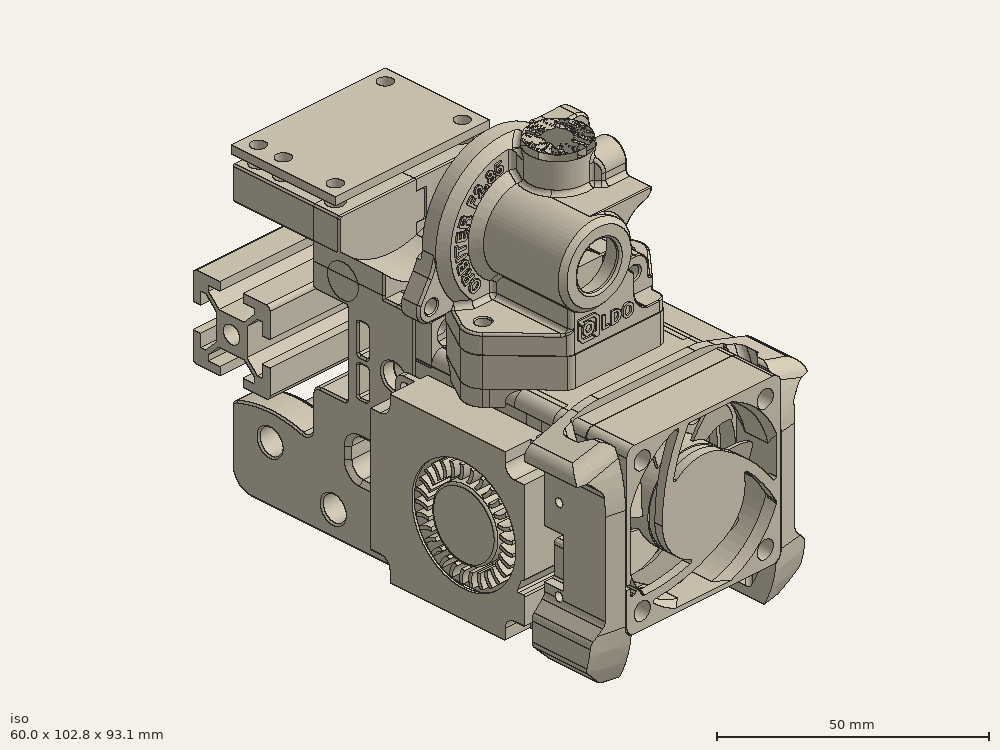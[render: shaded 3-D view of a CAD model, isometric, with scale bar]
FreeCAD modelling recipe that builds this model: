
FCSTD DOCUMENT  (FreeCAD 0.19R24291 (Git))
Label: dual4010-orbitor
License: Other
LicenseURL: GPL3
objects: Part::Cylinder×59, Part::MultiFuse×51, Part::Cut×51, Part::Box×46, Part::Feature×33, Part::Fillet×9, Part::Chamfer×9, Mesh::Feature×1, Part::Extrusion×1, Part::MultiCommon×1
note: 260 computed .brp shape members not serialized (recipe doc carries the construction recipe); baked Part::Feature solids carry a one-line shape summary decoded from their .brp

FEATURE [Part::Feature] Part__Feature376001  label="Left"
  shape: bbox 22.08 x 49.92 x 69.17 mm, 332 faces (baked)
FEATURE [Part::Feature] Part__Feature377001  label="Right"
  shape: bbox 22.32 x 49.92 x 69.17 mm, 357 faces (baked)
FEATURE [Part::Feature] Fusion003  label="mosquito"
  Placement = pos=(9e-15,-17.6,10) rot=(0.57735,0.57735,0.57735;2.0944rad)
  shape: bbox 27 x 18.85 x 47 mm, 463 faces, 0 solids (baked)
FEATURE [Part::Feature] Fusion036012039008  label="_2510-fan-pref"
  Placement = pos=(0.02,-24.2,26) rot=(1,0,0;1.5708rad)
  shape: bbox 25.76 x 10.5 x 25.8 mm, 132 faces, 2 solids (baked)
FEATURE [Part::Feature] Fusion001001  label="4010-fan"
  Placement = pos=(-19.9,-18.6,4.7) rot=(0,0,-1;1.5708rad)
  shape: bbox 10 x 40 x 40 mm, 256 faces, 2 solids (baked)
FEATURE [Part::Feature] Fusion036012039009  label="4010-fan001"
  Placement = pos=(19.9,-18.5,4.6) rot=(0,0,1;1.5708rad)
  shape: bbox 10 x 40 x 40 mm, 256 faces, 2 solids (baked)
FEATURE [Mesh::Feature] orbitor2
  Placement = pos=(-6.35,-7.9,74.9) rot=(0,0,1;0rad)
FEATURE [Part::Feature] Part__Feature013001  label="Cooling Fan Duct Focussed Edition_003"
  shape: bbox 15.53 x 56.74 x 51.73 mm, 120 faces (baked)
FEATURE [Part::Feature] Part__Feature012001  label="Cooling Fan Duct Focussed Edition001"
  shape: bbox 15.53 x 56.74 x 51.73 mm, 120 faces (baked)
FEATURE [Part::Feature] Part__Feature014001001  label="V6 Toolhead Mount 005"
  Placement = pos=(-0.05,0,0) rot=(0,0,1;0rad)
  shape: bbox 51.21 x 26.02 x 49.91 mm, 255 faces (baked)
FEATURE [Part::Box] Box  label="Cube"
  AttacherType = Attacher::AttachEngine3D
  Height = 10
  Length = 66
  Placement = pos=(-34,-27,49.86) rot=(0,0,1;0rad)
  Width = 34
FEATURE [Part::Box] Box002  label="Cube001"
  AttacherType = Attacher::AttachEngine3D
  Height = 10
  Length = 10
  Placement = pos=(-30,-23,41) rot=(0,0,1;0rad)
  Width = 26
FEATURE [Part::Box] Box004  label="Cube003"
  AttacherType = Attacher::AttachEngine3D
  Height = 10
  Length = 10
  Placement = pos=(20,-23,41) rot=(0,0,1;0rad)
  Width = 26
FEATURE [Part::Box] Box005  label="Cube004"
  AttacherType = Attacher::AttachEngine3D
  Height = 5.59
  Length = 24
  Placement = pos=(-12,-21.61,44.26) rot=(0,0,1;0rad)
  Width = 21.6
FEATURE [Part::Box] Box009  label="Cube008"
  AttacherType = Attacher::AttachEngine3D
  Height = 1.5
  Length = 24
  Placement = pos=(-12,-21.61,10.56) rot=(0,0,1;0rad)
  Width = 16
FEATURE [Part::Box] Box010  label="Cube009"
  AttacherType = Attacher::AttachEngine3D
  Height = 10
  Length = 25.3
  Placement = pos=(-12.65,-26.15,9.85) rot=(0,0,1;0rad)
  Width = 15
FEATURE [Part::Box] Box007  label="Cube006"
  AttacherType = Attacher::AttachEngine3D
  Height = 6
  Length = 30.3
  Placement = pos=(-15.15,-21.61,38.5) rot=(0,0,1;0rad)
  Width = 21.6
FEATURE [Part::Cylinder] Cylinder
  Angle = 360
  AttacherType = Attacher::AttachEngine3D
  Height = 22
  Placement = pos=(0,-17.6,33) rot=(0,0,1;0rad)
  Radius = 2.15
FEATURE [Part::Cylinder] Cylinder001
  Angle = 360
  AttacherType = Attacher::AttachEngine3D
  Height = 5
  Placement = pos=(-6,-17.6,33) rot=(0,0,1;0rad)
  Radius = 2.7
FEATURE [Part::Cylinder] Cylinder002
  Angle = 360
  AttacherType = Attacher::AttachEngine3D
  Height = 5
  Placement = pos=(6,-17.6,33) rot=(0,0,1;0rad)
  Radius = 2.7
FEATURE [Part::Cylinder] Cylinder003
  Angle = 360
  AttacherType = Attacher::AttachEngine3D
  Height = 22
  Placement = pos=(6,-17.6,33) rot=(0,0,1;0rad)
  Radius = 1.3
FEATURE [Part::Cylinder] Cylinder004
  Angle = 360
  AttacherType = Attacher::AttachEngine3D
  Height = 22
  Placement = pos=(-6,-17.6,33) rot=(0,0,1;0rad)
  Radius = 1.3
FEATURE [Part::MultiFuse] Fusion036012039011
  Shapes = -> [Cylinder,Cylinder003,Cylinder004]
FEATURE [Part::MultiFuse] Fusion036012039012
  Placement = pos=(0,0,11.9) rot=(0,0,1;0rad)
  Shapes = -> [Cylinder001,Cylinder002]
FEATURE [Part::Box] Box011  label="Cube010"
  AttacherType = Attacher::AttachEngine3D
  Height = 4.5
  Length = 12.15
  Placement = pos=(-18.65,-11.15,14) rot=(0,0,1;0rad)
  Width = 11.14
FEATURE [Part::Box] Box012  label="Cube011"
  AttacherType = Attacher::AttachEngine3D
  Height = 4.5
  Length = 12.15
  Placement = pos=(6.5,-11.15,14) rot=(0,0,1;0rad)
  Width = 11.14
FEATURE [Part::Box] Box013  label="Cube012"
  AttacherType = Attacher::AttachEngine3D
  Height = 10
  Length = 23.6
  Placement = pos=(-11.8,-22,4) rot=(0,0,1;0rad)
  Width = 11
FEATURE [Part::Fillet] Fillet
  Base = -> Box013
  Edges = 2 edges r=3: [Edge3,Edge7]
  Placement = pos=(0,2,0) rot=(0,0,1;0rad)
FEATURE [Part::Cylinder] Cylinder005
  Angle = 360
  AttacherType = Attacher::AttachEngine3D
  Height = 7
  Placement = pos=(16.1,-35.5,14.36) rot=(1,0,0;1.5708rad)
  Radius = 2.05
FEATURE [Part::Cylinder] Cylinder008
  Angle = 360
  AttacherType = Attacher::AttachEngine3D
  Height = 7
  Placement = pos=(-16.1,-35.5,14.36) rot=(1,0,0;1.5708rad)
  Radius = 2.05
FEATURE [Part::Cylinder] Cylinder009
  Angle = 360
  AttacherType = Attacher::AttachEngine3D
  Height = 8
  Placement = pos=(-16.1,-35.5,14.36) rot=(1,0,0;1.5708rad)
  Radius = 3.4
FEATURE [Part::Cylinder] Cylinder010
  Angle = 360
  AttacherType = Attacher::AttachEngine3D
  Height = 8
  Placement = pos=(-16.1,-35.5,46.21) rot=(1,0,0;1.5708rad)
  Radius = 3.4
FEATURE [Part::Cylinder] Cylinder011
  Angle = 360
  AttacherType = Attacher::AttachEngine3D
  Height = 8
  Placement = pos=(16.1,-35.5,46.21) rot=(1,0,0;1.5708rad)
  Radius = 3.4
FEATURE [Part::Cylinder] Cylinder012
  Angle = 360
  AttacherType = Attacher::AttachEngine3D
  Height = 8
  Placement = pos=(16.1,-35.5,14.36) rot=(1,0,0;1.5708rad)
  Radius = 3.4
FEATURE [Part::Cylinder] Cylinder013
  Angle = 360
  AttacherType = Attacher::AttachEngine3D
  Height = 21.6
  Placement = pos=(-16.1,-35.5,14.36) rot=(1,0,0;1.5708rad)
  Radius = 2
FEATURE [Part::Cylinder] Cylinder014
  Angle = 360
  AttacherType = Attacher::AttachEngine3D
  Height = 21.6
  Placement = pos=(-16.1,-35.5,46.21) rot=(1,0,0;1.5708rad)
  Radius = 2
FEATURE [Part::Cylinder] Cylinder015
  Angle = 360
  AttacherType = Attacher::AttachEngine3D
  Height = 21.6
  Placement = pos=(16.1,-35.5,46.21) rot=(1,0,0;1.5708rad)
  Radius = 2
FEATURE [Part::Cylinder] Cylinder016
  Angle = 360
  AttacherType = Attacher::AttachEngine3D
  Height = 21.6
  Placement = pos=(16.1,-35.5,14.36) rot=(1,0,0;1.5708rad)
  Radius = 2
FEATURE [Part::MultiFuse] Fusion036012039014
  Placement = pos=(0,35.49,0) rot=(0,0,1;0rad)
  Shapes = -> [Cylinder016,Cylinder015,Cylinder014,Cylinder013]
FEATURE [Part::MultiFuse] Fusion036012039016
  Placement = pos=(0,35.49,0) rot=(0,0,1;0rad)
  Shapes = -> [Cylinder012,Cylinder011,Cylinder010,Cylinder009]
FEATURE [Part::Cylinder] Cylinder017
  Angle = 360
  AttacherType = Attacher::AttachEngine3D
  Height = 10
  Placement = pos=(16.1,-35.5,14.36) rot=(1,0,0;1.5708rad)
  Radius = 1.7
FEATURE [Part::Cylinder] Cylinder019
  Angle = 360
  AttacherType = Attacher::AttachEngine3D
  Height = 10
  Placement = pos=(-16.1,-35.5,14.36) rot=(1,0,0;1.5708rad)
  Radius = 1.7
FEATURE [Part::Box] Box016  label="Cube015"
  AttacherType = Attacher::AttachEngine3D
  Height = 7
  Length = 1.2
  Placement = pos=(18.8,-21.61,42.8) rot=(0,0,1;0rad)
  Width = 14
FEATURE [Part::MultiFuse] Fusion036012039022
  Placement = pos=(0,23.89,0) rot=(0,0,1;0rad)
  Shapes = -> [Cylinder019,Cylinder017]
FEATURE [Part::MultiFuse] Fusion036012039023
  Placement = pos=(0,20.89,0) rot=(0,0,1;0rad)
  Shapes = -> [Cylinder005,Cylinder008]
FEATURE [Part::Cylinder] Cylinder020
  Angle = 360
  AttacherType = Attacher::AttachEngine3D
  Height = 10
  Placement = pos=(17.05,7,34) rot=(0.57735,-0.57735,0.57735;2.0944rad)
  Radius = 2.05
FEATURE [Part::Cylinder] Cylinder021
  Angle = 360
  AttacherType = Attacher::AttachEngine3D
  Height = 10
  Placement = pos=(-17.05,7,34) rot=(0.57735,-0.57735,0.57735;2.0944rad)
  Radius = 2.05
FEATURE [Part::Cylinder] Cylinder022
  Angle = 360
  AttacherType = Attacher::AttachEngine3D
  Height = 22.2
  Placement = pos=(-17.05,0,34) rot=(0.57735,-0.57735,0.57735;2.0944rad)
  Radius = 1.65
FEATURE [Part::Cylinder] Cylinder023
  Angle = 360
  AttacherType = Attacher::AttachEngine3D
  Height = 22.2
  Placement = pos=(17.05,8e-15,34) rot=(0.57735,-0.57735,0.57735;2.0944rad)
  Radius = 1.65
FEATURE [Part::Cylinder] Cylinder024
  Angle = 360
  AttacherType = Attacher::AttachEngine3D
  Height = 16
  Placement = pos=(-17.05,0,34) rot=(0.57735,-0.57735,0.57735;2.0944rad)
  Radius = 4
FEATURE [Part::Cylinder] Cylinder025
  Angle = 360
  AttacherType = Attacher::AttachEngine3D
  Height = 16
  Placement = pos=(17.05,8e-15,34) rot=(0.57735,-0.57735,0.57735;2.0944rad)
  Radius = 4
FEATURE [Part::Cut] Cut009
  Base = -> Part__Feature376001
  Tool = -> Cylinder021
FEATURE [Part::Box] Box017  label="Cube016"
  AttacherType = Attacher::AttachEngine3D
  Height = 10
  Length = 10
  Placement = pos=(17.9,-16,29) rot=(0,0,1;0rad)
  Width = 26
FEATURE [Part::Box] Box018  label="Cube017"
  AttacherType = Attacher::AttachEngine3D
  Height = 10
  Length = 10
  Placement = pos=(-27.9,-16,29) rot=(0,0,1;0rad)
  Width = 26
FEATURE [Part::MultiFuse] Fusion036012039026
  Shapes = -> [Box017,Box018]
FEATURE [Part::Cut] Cut
  Base = -> Part__Feature014001001
  Tool = -> Box
FEATURE [Part::MultiFuse] Fusion036012039033
  Shapes = -> [Box011,Box012]
FEATURE [Part::Cylinder] Cylinder030
  Angle = 360
  AttacherType = Attacher::AttachEngine3D
  Height = 11
  Placement = pos=(16.25,11,9.41) rot=(1,0,0;1.5708rad)
  Radius = 2.5
FEATURE [Part::Cylinder] Cylinder031
  Angle = 360
  AttacherType = Attacher::AttachEngine3D
  Height = 11
  Placement = pos=(-16.25,11,9.41) rot=(1,0,0;1.5708rad)
  Radius = 2.5
FEATURE [Part::MultiFuse] Fusion036012039039
  Shapes = -> [Cut009,Cylinder031]
FEATURE [Part::Box] Box019  label="Cube018"
  AttacherType = Attacher::AttachEngine3D
  Height = 10
  Length = 8.8
  Placement = pos=(11.2,-5,5) rot=(0,0,1;0rad)
  Width = 5
FEATURE [Part::Box] Box020  label="Cube019"
  AttacherType = Attacher::AttachEngine3D
  Height = 10
  Length = 8.8
  Placement = pos=(-20,-5,5) rot=(0,0,1;0rad)
  Width = 5
FEATURE [Part::Chamfer] Chamfer002
  Base = -> Box019
  Edges = 5 edges r=0.4: [Edge3,Edge4,Edge7,Edge8,Edge11]
FEATURE [Part::Chamfer] Chamfer003
  Base = -> Box020
  Edges = 5 edges r=0.4: [Edge3,Edge4,Edge7,Edge8,Edge11]
FEATURE [Part::Box] Box021  label="Cube020"
  AttacherType = Attacher::AttachEngine3D
  Height = 10
  Length = 26
  Placement = pos=(-13,-10,10.6) rot=(0,0,1;0rad)
  Width = 10
FEATURE [Part::Cylinder] Cylinder032
  Angle = 360
  AttacherType = Attacher::AttachEngine3D
  Height = 10
  Placement = pos=(-15.6,7,7.5) rot=(0.57735,-0.57735,0.57735;2.0944rad)
  Radius = 2.05
FEATURE [Part::Cylinder] Cylinder033
  Angle = 360
  AttacherType = Attacher::AttachEngine3D
  Height = 10
  Placement = pos=(15.6,7,7.5) rot=(0.57735,-0.57735,0.57735;2.0944rad)
  Radius = 2.05
FEATURE [Part::Cylinder] Cylinder034
  Angle = 360
  AttacherType = Attacher::AttachEngine3D
  Height = 10
  Placement = pos=(-15.6,2e-15,7.5) rot=(0.57735,-0.57735,0.57735;2.0944rad)
  Radius = 1.65
FEATURE [Part::Cylinder] Cylinder035
  Angle = 360
  AttacherType = Attacher::AttachEngine3D
  Height = 10
  Placement = pos=(15.6,0,7.5) rot=(0.57735,-0.57735,0.57735;2.0944rad)
  Radius = 1.65
FEATURE [Part::MultiFuse] Fusion036012039042
  Placement = pos=(0,3,0) rot=(0,0,1;0rad)
  Shapes = -> [Cylinder035,Cylinder034]
FEATURE [Part::MultiFuse] Fusion036012039043
  Shapes = -> [Chamfer003,Chamfer002]
FEATURE [Part::Cut] Cut021
  Base = -> Fusion036012039043
  Tool = -> Box021
FEATURE [Part::Cut] Cut023
  Base = -> Fusion036012039039
  Tool = -> Cylinder032
FEATURE [Part::Box] Box023  label="Cube022"
  AttacherType = Attacher::AttachEngine3D
  Height = 10
  Length = 3.3
  Placement = pos=(-17.25,-6,-2.5) rot=(0,0,1;0rad)
  Width = 10
FEATURE [Part::Box] Box024  label="Cube023"
  AttacherType = Attacher::AttachEngine3D
  Height = 10
  Length = 3.3
  Placement = pos=(13.95,-8,-2.5) rot=(0,0,1;0rad)
  Width = 10
FEATURE [Part::MultiFuse] Fusion036012039045
  Shapes = -> [Box023,Box024]
FEATURE [Part::MultiFuse] Fusion036012039029004
  Shapes = -> [Fusion036012039045,Fusion036012039042]
FEATURE [Part::Box] Box028  label="Cube027"
  AttacherType = Attacher::AttachEngine3D
  Height = 4
  Length = 2
  Placement = pos=(18,-25,16) rot=(0,0,1;0rad)
  Width = 22
FEATURE [Part::Fillet] Fillet001
  Base = -> Box028
  Edges = 2 edges r=1: [Edge11,Edge12]
  Placement = pos=(0.8,-0.6,0) rot=(0,0,1;0rad)
FEATURE [Part::Box] Box030  label="Cube029"
  AttacherType = Attacher::AttachEngine3D
  Height = 28
  Length = 1.2
  Placement = pos=(18.8,-21.61,15.8) rot=(0,0,1;0rad)
  Width = 18
FEATURE [Part::Box] Box031  label="Cube030"
  AttacherType = Attacher::AttachEngine3D
  Height = 8
  Length = 2
  Placement = pos=(18.8,-7.61,17.9) rot=(0,0,1;0rad)
  Width = 4
FEATURE [Part::Feature] Part__Feature034  label="4010-fan002"
  Placement = pos=(-19.975,-55.3,50.05) rot=(0.57735,0.57735,-0.57735;2.0944rad)
  shape: bbox 40.01 x 10.74 x 40.01 mm, 116 faces (baked)
FEATURE [Part::Cylinder] Cylinder037
  Angle = 360
  AttacherType = Attacher::AttachEngine3D
  Height = 20
  Placement = pos=(-9e-15,18.55,55.65) rot=(0.707107,0,0.707107;3.14159rad)
  Radius = 4
FEATURE [Part::Cylinder] Cylinder038
  Angle = 360
  AttacherType = Attacher::AttachEngine3D
  Height = 20
  Placement = pos=(-20,18.55,55.65) rot=(0.707107,0,0.707107;3.14159rad)
  Radius = 4
FEATURE [Part::MultiFuse] Fusion036012039029011  label="Fusion036012039029012"
  Shapes = -> [Cut023,Cylinder038]
FEATURE [Part::Box] Box036  label="Cube035"
  AttacherType = Attacher::AttachEngine3D
  Height = 14
  Length = 60
  Placement = pos=(-30,19.3,56.3) rot=(0,0,1;0rad)
  Width = 36
FEATURE [Part::Feature] Chamfer008016001  label="m8-probe-mount001"
  Placement = pos=(0,10,3) rot=(0,0,1;0rad)
  shape: bbox 15 x 15.5 x 10 mm, 61 faces (baked)
FEATURE [Part::Box] Box040  label="Cube039"
  AttacherType = Attacher::AttachEngine3D
  Height = 9.8
  Length = 9.2
  Placement = pos=(-20,-4.51,46.5) rot=(0,0,1;0rad)
  Width = 4.5
FEATURE [Part::Box] Box041  label="Cube040"
  AttacherType = Attacher::AttachEngine3D
  Height = 9.8
  Length = 9.2
  Placement = pos=(10.8,-4.51,46.5) rot=(0,0,1;0rad)
  Width = 4.5
FEATURE [Part::Box] Box042  label="Cube041"
  AttacherType = Attacher::AttachEngine3D
  Height = 14
  Length = 21.6
  Placement = pos=(-10.8,-10.95,38) rot=(0,0,1;0rad)
  Width = 15
FEATURE [Part::Box] Box043  label="Cube042"
  AttacherType = Attacher::AttachEngine3D
  Height = 10
  Length = 10
  Placement = pos=(-27,-23,46.86) rot=(0,0,1;0rad)
  Width = 24
FEATURE [Part::Box] Box044  label="Cube043"
  AttacherType = Attacher::AttachEngine3D
  Height = 10
  Length = 10
  Placement = pos=(17,-23,46.86) rot=(0,0,1;0rad)
  Width = 24
FEATURE [Part::Box] Box045  label="Cube044"
  AttacherType = Attacher::AttachEngine3D
  Height = 10
  Length = 10
  Placement = pos=(-20,-23,39.86) rot=(0,0,1;0rad)
  Width = 24
FEATURE [Part::Box] Box046  label="Cube045"
  AttacherType = Attacher::AttachEngine3D
  Height = 10
  Length = 10
  Placement = pos=(10,-23,39.86) rot=(0,0,1;0rad)
  Width = 24
FEATURE [Part::Fillet] Fillet001005
  Base = -> Box045
  Edges = 1 edges r=2.8: [Edge2]
FEATURE [Part::Fillet] Fillet001006
  Base = -> Box046
  Edges = 1 edges r=2.8: [Edge6]
FEATURE [Part::Cut] Cut011025
  Base = -> Box043
  Tool = -> Fillet001005
FEATURE [Part::Cut] Cut011026
  Base = -> Box044
  Tool = -> Fillet001006
FEATURE [Part::MultiFuse] Fusion036012039029016  label="Fusion036012039029017"
  Shapes = -> [Cut011026,Cut011025]
FEATURE [Part::Chamfer] Chamfer008016002
  Base = -> Box041
  Edges = 5 edges r=0.4: [Edge2,Edge3,Edge6,Edge7,Edge12]
FEATURE [Part::Chamfer] Chamfer008016003
  Base = -> Box040
  Edges = 5 edges r=0.4: [Edge2,Edge3,Edge6,Edge7,Edge12]
FEATURE [Part::MultiFuse] Fusion036012039029017  label="Fusion036012039029018"
  Shapes = -> [Chamfer008016002,Chamfer008016003]
FEATURE [Part::Cylinder] Cylinder041
  Angle = 360
  AttacherType = Attacher::AttachEngine3D
  Height = 10
  Placement = pos=(15.5,-2.5,52.71) rot=(1,0,0;1.5708rad)
  Radius = 3
FEATURE [Part::Cylinder] Cylinder042
  Angle = 360
  AttacherType = Attacher::AttachEngine3D
  Height = 10
  Placement = pos=(-15.5,-2.5,52.71) rot=(1,0,0;1.5708rad)
  Radius = 3
FEATURE [Part::Cylinder] Cylinder043
  Angle = 360
  AttacherType = Attacher::AttachEngine3D
  Height = 10
  Placement = pos=(-15.5,7,52.71) rot=(1,0,0;1.5708rad)
  Radius = 2.05
FEATURE [Part::Cylinder] Cylinder044
  Angle = 360
  AttacherType = Attacher::AttachEngine3D
  Height = 10
  Placement = pos=(15.5,7,52.71) rot=(1,0,0;1.5708rad)
  Radius = 2.05
FEATURE [Part::Cylinder] Cylinder045
  Angle = 360
  AttacherType = Attacher::AttachEngine3D
  Height = 10
  Placement = pos=(-15.5,1.2e-14,52.71) rot=(1,0,0;1.5708rad)
  Radius = 1.65
FEATURE [Part::Cylinder] Cylinder046
  Angle = 360
  AttacherType = Attacher::AttachEngine3D
  Height = 10
  Placement = pos=(15.5,1.2e-14,52.71) rot=(1,0,0;1.5708rad)
  Radius = 1.65
FEATURE [Part::Feature] Fillet001016001  label="front-body-r1"
  shape: bbox 104.4 x 16.9 x 53 mm, 125 faces (baked)
FEATURE [Part::Feature] Fillet001013001  label="fan-spacer-r1"
  shape: bbox 40 x 4 x 40 mm, 20 faces (baked)
FEATURE [Part::MultiFuse] Fusion
  Shapes = -> [Box002,Box004]
FEATURE [Part::Cut] Cut011033
  Base = -> Cut
  Tool = -> Fusion
FEATURE [Part::MultiFuse] Fusion036012039029018  label="Fusion036012039029019"
  Shapes = -> [Cut011033,Box005]
FEATURE [Part::MultiFuse] Fusion036012039029019  label="Fusion036012039029020"
  Shapes = -> [Box009,Fusion036012039029018]
FEATURE [Part::Cut] Cut011034
  Base = -> Fusion036012039029019
  Tool = -> Box010
FEATURE [Part::Chamfer] Chamfer
  Base = -> Fusion036012039033
  Edges = 2 edges r=5: [Edge7,Edge15]
FEATURE [Part::Chamfer] Chamfer008016004
  Base = -> Chamfer
  Edges = 2 edges r=0.4: [Edge3,Edge18]
FEATURE [Part::Box] Box047  label="Cube046"
  AttacherType = Attacher::AttachEngine3D
  Height = 8
  Length = 2
  Placement = pos=(18.8,-25.61,17.9) rot=(0,0,1;0rad)
  Width = 4
FEATURE [Part::Fillet] Fillet001016002
  Base = -> Box031
  Edges = 2 edges r=1: [Edge10,Edge12]
FEATURE [Part::MultiFuse] Fusion036012039029029  label="Fusion036012039029030"
  Shapes = -> [Fillet001,Box047,Fillet001016002]
FEATURE [Part::Fillet] Fillet001016003
  Base = -> Fusion036012039029029
  Edges = 2 edges r=1: [Edge11,Edge21]
FEATURE [Part::MultiFuse] Fusion036012039029031  label="Fusion036012039029032"
  Shapes = -> [Cylinder042,Cylinder041,Cylinder045,Cylinder046]
FEATURE [Part::Feature] Part__Feature082001  label="orbitor-front-body"
  Placement = pos=(-6.58,-4.85,74.86) rot=(0,0,1;3.14159rad)
  shape: bbox 135.7 x 30.33 x 139 mm, 688 faces (baked)
FEATURE [Part::Cylinder] Cylinder047
  Angle = 360
  AttacherType = Attacher::AttachEngine3D
  Height = 10
  Placement = pos=(-19.5,-17.6,46) rot=(0,0,1;0rad)
  Radius = 2
FEATURE [Part::Cylinder] Cylinder048
  Angle = 360
  AttacherType = Attacher::AttachEngine3D
  Height = 10
  Placement = pos=(17.5,-17.6,46) rot=(0,0,1;0rad)
  Radius = 2
FEATURE [Part::Feature] Face011
  shape: bbox 46 x 25.7 x 3e-07 mm, 1 faces, 0 solids (baked)
FEATURE [Part::Extrusion] Extrude  label="plate-template"
  Base = -> Face011
  Dir = (0,0,1)
  DirMode = 2
  FaceMakerClass = Part::FaceMakerBullseye
  LengthFwd = 11
  LengthRev = 0
  Placement = pos=(0,0,-12.5) rot=(0,0,1;0rad)
  Solid = false
  Symmetric = false
FEATURE [Part::Box] Box048  label="Cube047"
  AttacherType = Attacher::AttachEngine3D
  Height = 20
  Length = 66
  Placement = pos=(-30,-21.61,38) rot=(0,0,1;0rad)
  Width = 28
FEATURE [Part::Feature] Extrude001  label="plate-template001"
  Placement = pos=(0,0,-12.5) rot=(0,0,1;0rad)
  shape: bbox 46 x 25.7 x 11 mm, 14 faces (baked)
FEATURE [Part::Feature] Extrude002  label="plate-template002"
  Placement = pos=(0,0,-12.5) rot=(0,0,1;0rad)
  shape: bbox 46 x 25.7 x 11 mm, 14 faces (baked)
FEATURE [Part::Box] Box049  label="Cube048"
  AttacherType = Attacher::AttachEngine3D
  Height = 20
  Length = 66
  Placement = pos=(-30,-21.61,38) rot=(0,0,1;0rad)
  Width = 28
FEATURE [Part::MultiCommon] Common
  Shapes = -> [Extrude001,Box048]
FEATURE [Part::Cut] Cut011046
  Base = -> Extrude002
  Tool = -> Box049
FEATURE [Part::Box] Box050  label="Cube049"
  AttacherType = Attacher::AttachEngine3D
  Height = 20
  Length = 66
  Placement = pos=(-30,-34.61,49.86) rot=(0,0,1;0rad)
  Width = 41
FEATURE [Part::Box] Box051  label="Cube050"
  AttacherType = Attacher::AttachEngine3D
  Height = 20
  Length = 66
  Placement = pos=(-30,-34.61,49.86) rot=(0,0,1;0rad)
  Width = 41
FEATURE [Part::Cut] Cut011047
  Base = -> Cut011046
  Tool = -> Box051
FEATURE [Part::Cut] Cut011048
  Base = -> Common
  Tool = -> Box050
FEATURE [Part::Cylinder] Cylinder049
  Angle = 360
  AttacherType = Attacher::AttachEngine3D
  Height = 20
  Placement = pos=(-16,-20.28,46.2) rot=(1,0,0;1.5708rad)
  Radius = 3
FEATURE [Part::Cylinder] Cylinder050
  Angle = 360
  AttacherType = Attacher::AttachEngine3D
  Height = 20
  Placement = pos=(16,-20.28,46.2) rot=(1,0,0;1.5708rad)
  Radius = 3
FEATURE [Part::MultiFuse] Fusion036012039029032  label="Fusion036012039029033"
  Shapes = -> [Cylinder049,Cylinder050]
FEATURE [Part::Cut] Cut011049
  Base = -> Cut011047
  Tool = -> Fusion036012039029032
FEATURE [Part::Box] Box052  label="Cube051"
  AttacherType = Attacher::AttachEngine3D
  Height = 15
  Length = 19
  Placement = pos=(-9.4,-21.5,37.6) rot=(0,0,1;0rad)
  Width = 9
FEATURE [Part::Cut] Cut011050
  Base = -> Cut011048
  Tool = -> Box052
FEATURE [Part::Box] Box053  label="Cube052"
  AttacherType = Attacher::AttachEngine3D
  Height = 10
  Length = 21.6
  Placement = pos=(-10.8,-10.95,43.1) rot=(0,0,1;0rad)
  Width = 10
FEATURE [Part::Chamfer] Chamfer008016008
  Base = -> Box053
  Edges = 2 edges r=2: [Edge1,Edge5]
FEATURE [Part::Cut] Cut011051
  Base = -> Cut011050
  Tool = -> Chamfer008016008
FEATURE [Part::Box] Box054  label="Cube053"
  AttacherType = Attacher::AttachEngine3D
  Height = 10
  Length = 3
  Placement = pos=(-16.8,-12.6,47.8) rot=(0,0,1;0rad)
  Width = 10
FEATURE [Part::Box] Box055  label="Cube054"
  AttacherType = Attacher::AttachEngine3D
  Height = 10
  Length = 3
  Placement = pos=(13.6,-12.6,47.8) rot=(0,0,1;0rad)
  Width = 10
FEATURE [Part::MultiFuse] Fusion036012039029034  label="Fusion036012039029035"
  Shapes = -> [Box054,Box055]
FEATURE [Part::Cut] Cut011052
  Base = -> Cut011051
  Tool = -> Fusion036012039029034
FEATURE [Part::Cylinder] Cylinder051
  Angle = 360
  AttacherType = Attacher::AttachEngine3D
  Height = 18
  Placement = pos=(0,-17.6,41.6) rot=(0,0,1;0rad)
  Radius = 2.1
FEATURE [Part::Cylinder] Cylinder052
  Angle = 360
  AttacherType = Attacher::AttachEngine3D
  Height = 15
  Placement = pos=(17.5,-17.6,44) rot=(0,0,1;0rad)
  Radius = 1.65
FEATURE [Part::Cylinder] Cylinder053
  Angle = 360
  AttacherType = Attacher::AttachEngine3D
  Height = 15
  Placement = pos=(-19.5,-17.6,44) rot=(0,0,1;0rad)
  Radius = 1.65
FEATURE [Part::MultiFuse] Fusion036012039029036  label="Fusion036012039029037"
  Shapes = -> [Cylinder048,Cylinder047]
FEATURE [Part::Cylinder] Cylinder054
  Angle = 360
  AttacherType = Attacher::AttachEngine3D
  Height = 18
  Placement = pos=(0,-27.6,44.6) rot=(0,0,1;0rad)
  Radius = 2
FEATURE [Part::Cylinder] Cylinder055
  Angle = 360
  AttacherType = Attacher::AttachEngine3D
  Height = 15
  Placement = pos=(0,-27.6,44.6) rot=(0,0,1;0rad)
  Radius = 1.65
FEATURE [Part::Feature] CFFFP_plate_template001001_solid  label="plate-inner"
  Placement = pos=(0,-19.75,49.4) rot=(0,0,1;0rad)
  shape: bbox 34.49 x 19.28 x 8.25 mm, 38 faces (baked)
FEATURE [Part::Cylinder] Cylinder056
  Angle = 360
  AttacherType = Attacher::AttachEngine3D
  Height = 10
  Placement = pos=(0,-18,39.86) rot=(0,0,1;0rad)
  Radius = 27
FEATURE [Part::Cut] Cut011055
  Base = -> Extrude
  Tool = -> Cylinder056
FEATURE [Part::Cylinder] Cylinder057
  Angle = 360
  AttacherType = Attacher::AttachEngine3D
  Height = 15
  Placement = pos=(0,-27.6,44.6) rot=(0,0,1;0rad)
  Radius = 5
FEATURE [Part::Cylinder] Cylinder058
  Angle = 360
  AttacherType = Attacher::AttachEngine3D
  Height = 15
  Placement = pos=(-19.5,-17.6,44) rot=(0,0,1;0rad)
  Radius = 5
FEATURE [Part::Cylinder] Cylinder059
  Angle = 360
  AttacherType = Attacher::AttachEngine3D
  Height = 15
  Placement = pos=(17.5,-17.6,44) rot=(0,0,1;0rad)
  Radius = 5
FEATURE [Part::Cylinder] Cylinder060
  Angle = 360
  AttacherType = Attacher::AttachEngine3D
  Height = 18
  Placement = pos=(0,-17.6,41.6) rot=(0,0,1;0rad)
  Radius = 4
FEATURE [Part::MultiFuse] Fusion036012039029037  label="Fusion036012039029038"
  Shapes = -> [Cylinder058,Cylinder057,Cylinder060,Cylinder059]
FEATURE [Part::Cut] Cut011056
  Base = -> CFFFP_plate_template001001_solid
  Tool = -> Fusion036012039029037
FEATURE [Part::Box] Box056  label="Cube055"
  AttacherType = Attacher::AttachEngine3D
  Height = 10
  Length = 30
  Placement = pos=(-15.7,-20.1,48.2) rot=(0,0,1;0rad)
  Width = 5
FEATURE [Part::Box] Box057  label="Cube056"
  AttacherType = Attacher::AttachEngine3D
  Height = 10
  Length = 5
  Placement = pos=(-2.5,-25,48.2) rot=(0,0,1;0rad)
  Width = 16
FEATURE [Part::MultiFuse] Fusion036012039029038  label="Fusion036012039029039"
  Shapes = -> [Box056,Box057]
FEATURE [Part::Cut] Cut011057
  Base = -> Cut011056
  Tool = -> Fusion036012039029038
FEATURE [Part::Cut] Cut011058
  Base = -> Cut011055
  Tool = -> Cut011057
FEATURE [Part::Cylinder] Cylinder061
  Angle = 360
  AttacherType = Attacher::AttachEngine3D
  Height = 15
  Placement = pos=(0,-27.6,53.5) rot=(0,0,1;0rad)
  Radius = 3.5
FEATURE [Part::Cut] Cut011059
  Base = -> Cut011058
  Tool = -> Cylinder061
FEATURE [Part::MultiFuse] Fusion036012039029039  label="Fusion036012039029040"
  Shapes = -> [Cylinder053,Cylinder051,Cylinder055,Cylinder052]
FEATURE [Part::Cut] Cut011060  label="raiser-r1"
  Base = -> Cut011059
  Tool = -> Fusion036012039029039
FEATURE [Part::Cut] Cut011029
  Base = -> Fusion036012039029011
  Tool = -> Cylinder043
FEATURE [Part::Feature] Fusion036012039029022001  label="Fusion036012039029041"
  Placement = pos=(0,70.7,45) rot=(0,0,1;0rad)
  shape: bbox 7 x 18.5 x 30 mm, 10 faces (baked)
FEATURE [Part::Feature] Chamfer008016008001  label="Chamfer008016013"
  shape: bbox 20 x 18.8 x 12 mm, 13 faces (baked)
FEATURE [Part::Feature] Chamfer008016007001  label="Chamfer008016012"
  shape: bbox 20 x 18.8 x 12 mm, 13 faces (baked)
FEATURE [Part::Feature] Fusion036012039029022002  label="Fusion036012039029042"
  Placement = pos=(0,70.7,45) rot=(0,0,1;0rad)
  shape: bbox 7 x 18.5 x 30 mm, 10 faces (baked)
FEATURE [Part::MultiFuse] Fusion036012039029022003
  Shapes = -> [Chamfer008016007001,Cut011029]
FEATURE [Part::Cut] Cut011061
  Base = -> Fusion036012039029022003
  Tool = -> Fusion036012039029022001
FEATURE [Part::Cylinder] Cylinder062
  Angle = 360
  AttacherType = Attacher::AttachEngine3D
  Height = 16
  Placement = pos=(-6.5,19.3,74.9) rot=(1,0,0;1.5708rad)
  Radius = 19
FEATURE [Part::Cylinder] Cylinder063
  Angle = 360
  AttacherType = Attacher::AttachEngine3D
  Height = 16
  Placement = pos=(-6.5,19.3,74.9) rot=(1,0,0;1.5708rad)
  Radius = 19
FEATURE [Part::Cut] Cut011063
  Base = -> Cut011061
  Tool = -> Cylinder062
FEATURE [Part::Box] Box058  label="Cube057"
  AttacherType = Attacher::AttachEngine3D
  Height = 14
  Length = 60
  Placement = pos=(-30,19.3,56.3) rot=(0,0,1;0rad)
  Width = 36
FEATURE [Part::Feature] Fusion036012039029014001  label="Fusion036012039029022005"
  Placement = pos=(0,4.8,1.3) rot=(0,0,1;0rad)
  shape: bbox 34 x 4 x 10 mm, 6 faces, 2 solids (baked)
FEATURE [Part::Feature] Cut011069020001  label="body-mid-r002"
  shape: bbox 44.57 x 17.46 x 39.3 mm, 137 faces (baked)
FEATURE [Part::MultiFuse] Fusion036012039029022005  label="Fusion036012039029022006"
  Shapes = -> [Cut011049,Cut011069020001]
FEATURE [Part::Cut] Cut011069020002  label="mid-body-r1"
  Base = -> Fusion036012039029022005
  Tool = -> Cylinder054
FEATURE [Part::Cut] Cut011069020003
  Base = -> Part__Feature377001
  Tool = -> Cylinder020
FEATURE [Part::MultiFuse] Fusion036012039029022006  label="Fusion036012039029022007"
  Shapes = -> [Cylinder030,Cut011069020003]
FEATURE [Part::Cut] Cut011069020004
  Base = -> Fusion036012039029022006
  Tool = -> Cylinder033
FEATURE [Part::MultiFuse] Fusion036012039029022007  label="Fusion036012039029022008"
  Shapes = -> [Cylinder037,Cut011069020004]
FEATURE [Part::Cut] Cut011069020005
  Base = -> Fusion036012039029022007
  Tool = -> Cylinder044
FEATURE [Part::MultiFuse] Fusion036012039029022008  label="Fusion036012039029022009"
  Shapes = -> [Chamfer008016008001,Cut011069020005]
FEATURE [Part::Cut] Cut011069020006
  Base = -> Fusion036012039029022008
  Tool = -> Fusion036012039029022002
FEATURE [Part::Cut] Cut011069020007
  Base = -> Cut011069020006
  Tool = -> Cylinder063
FEATURE [Part::MultiFuse] Fusion036012039029022009  label="Fusion036012039029022010"
  Shapes = -> [Cylinder024,Cylinder025]
FEATURE [Part::Cut] Cut011069020011
  Base = -> Fusion036012039029022009
  Tool = -> Fusion036012039026
FEATURE [Part::Feature] Cut011069020011001  label="Cut011069020012"
  Placement = pos=(0,-5.61,0) rot=(0,0,1;0rad)
  shape: bbox 35.8 x 16 x 8 mm, 10 faces, 2 solids (baked)
FEATURE [Part::MultiFuse] Fusion036012039029022010  label="Fusion036012039029022011"
  Shapes = -> [Cut011069020011001,Cut011069020011]
FEATURE [Part::MultiFuse] Fusion036012039029022011  label="Fusion036012039029022012"
  Shapes = -> [Cut011034,Box007]
FEATURE [Part::Cut] Cut011069020011002
  Base = -> Fusion036012039029022011
  Tool = -> Fusion036012039011
FEATURE [Part::Cut] Cut011069020011003
  Base = -> Cut011069020011002
  Tool = -> Fusion036012039012
FEATURE [Part::MultiFuse] Fusion036012039029022012  label="Fusion036012039029022013"
  Shapes = -> [Chamfer008016004,Cut011069020011003]
FEATURE [Part::Cut] Cut011069020011004
  Base = -> Fusion036012039029022012
  Tool = -> Fillet
FEATURE [Part::MultiFuse] Fusion036012039029022013  label="Fusion036012039029022014"
  Shapes = -> [Fusion036012039016,Fusion036012039014]
FEATURE [Part::MultiFuse] Fusion036012039029022014  label="Fusion036012039029022015"
  Shapes = -> [Cut011069020011004,Fusion036012039029022013]
FEATURE [Part::Cut] Cut011069020011005
  Base = -> Fusion036012039029022014
  Tool = -> Fusion036012039022
FEATURE [Part::Cut] Cut011069020011006
  Base = -> Cut011069020011005
  Tool = -> Fusion036012039023
FEATURE [Part::MultiFuse] Fusion036012039029022015  label="Fusion036012039029022016"
  Shapes = -> [Box016,Cut011069020011006]
FEATURE [Part::MultiFuse] Fusion036012039029022016  label="Fusion036012039029022017"
  Shapes = -> [Fusion036012039029022010,Fusion036012039029022015]
FEATURE [Part::MultiFuse] Fusion036012039029022017  label="Fusion036012039029022018"
  Shapes = -> [Cylinder023,Cylinder022]
FEATURE [Part::Cut] Cut011069020011007
  Base = -> Fusion036012039029022016
  Tool = -> Fusion036012039029022017
FEATURE [Part::MultiFuse] Fusion036012039029022018  label="Fusion036012039029022019"
  Shapes = -> [Cut011069020011007,Cut021]
FEATURE [Part::Cut] Cut011069020011008
  Base = -> Fusion036012039029022018
  Tool = -> Fusion036012039029004
FEATURE [Part::MultiFuse] Fusion036012039029022019  label="Fusion036012039029022020"
  Shapes = -> [Box030,Cut011069020011008]
FEATURE [Part::Cut] Cut011069020011009
  Base = -> Fusion036012039029022019
  Tool = -> Fillet001016003
FEATURE [Part::Cut] Cut011069020011010
  Base = -> Cut011069020011009
  Tool = -> Fusion036012039029016
FEATURE [Part::Cut] Cut011069020011011
  Base = -> Cut011069020011010
  Tool = -> Box042
FEATURE [Part::Chamfer] Chamfer008016008002
  Base = -> Cut011069020011011
  Edges = 2 edges r=0.4: [Edge443,Edge459]
FEATURE [Part::Chamfer] Chamfer008016008003
  Base = -> Chamfer008016008002
  Edges = 2 edges r=2: [Edge37,Edge42]
FEATURE [Part::MultiFuse] Fusion036012039029022020  label="Fusion036012039029022021"
  Shapes = -> [Chamfer008016008003,Fusion036012039029017]
FEATURE [Part::Cut] Cut011069020011012
  Base = -> Fusion036012039029022020
  Tool = -> Fusion036012039029031
FEATURE [Part::MultiFuse] Fusion036012039029022021  label="Fusion036012039029022022"
  Shapes = -> [Cut011052,Cut011069020011012]
FEATURE [Part::Cut] Cut011069020011013  label="back-body-r1"
  Base = -> Fusion036012039029022021
  Tool = -> Fusion036012039029036
FEATURE [Part::Feature] Common001  label="2020-extrusion"
  Placement = pos=(0,27.5,30.6) rot=(0,0,1;0rad)
  shape: bbox 60 x 20 x 20 mm, 51 faces (baked)
FEATURE [Part::Feature] Cut036009013017007008008021005005044017001001  label="Cut036009013017007008008021005005044017003"
  shape: bbox 2.602 x 8 x 8 mm, 15 faces (baked)
FEATURE [Part::Feature] Chamfer008016008005002001  label="Chamfer008016008005003"
  shape: bbox 2 x 4 x 4 mm, 4 faces (baked)
FEATURE [Part::Feature] Cylinder073001  label="Cylinder074"
  Placement = pos=(2.2,43,64.76) rot=(0,-1,0;1.5708rad)
  shape: bbox 2.2 x 4.3 x 4.3 mm, 3 faces (baked)
FEATURE [Part::Feature] Cut011069020011016001  label="PCB-template001"
  shape: bbox 40 x 27 x 2 mm, 11 faces (baked)
FEATURE [Part::Feature] Chamfer008016008004001  label="Chamfer008016008006"
  shape: bbox 20 x 35 x 8 mm, 13 faces (baked)
FEATURE [Part::Feature] Chamfer008016008005001  label="Chamfer008016008007"
  shape: bbox 20 x 35 x 8 mm, 13 faces (baked)
FEATURE [Part::Cylinder] Cylinder071
  Angle = 360
  AttacherType = Attacher::AttachEngine3D
  Height = 10
  Placement = pos=(-16.5,37.5,60) rot=(0,0,1;0rad)
  Radius = 2
FEATURE [Part::Cylinder] Cylinder067
  Angle = 360
  AttacherType = Attacher::AttachEngine3D
  Height = 10
  Placement = pos=(16.5,24,60) rot=(0,0,1;0rad)
  Radius = 2
FEATURE [Part::Cylinder] Cylinder066
  Angle = 360
  AttacherType = Attacher::AttachEngine3D
  Height = 10
  Placement = pos=(-16.5,24,60) rot=(0,0,1;0rad)
  Radius = 2
FEATURE [Part::Cylinder] Cylinder064
  Angle = 360
  AttacherType = Attacher::AttachEngine3D
  Height = 10
  Placement = pos=(16.5,44,60) rot=(0,0,1;0rad)
  Radius = 2
FEATURE [Part::Cylinder] Cylinder065
  Angle = 360
  AttacherType = Attacher::AttachEngine3D
  Height = 10
  Placement = pos=(-16.5,44,60) rot=(0,0,1;0rad)
  Radius = 2
FEATURE [Part::Box] Box059  label="Cube058"
  AttacherType = Attacher::AttachEngine3D
  Height = 10
  Length = 40
  Placement = pos=(-20,12,59) rot=(0,0,1;0rad)
  Width = 8
FEATURE [Part::Box] Box060  label="Cube059"
  AttacherType = Attacher::AttachEngine3D
  Height = 10
  Length = 40
  Placement = pos=(-20,12,59) rot=(0,0,1;0rad)
  Width = 8
FEATURE [Part::Cut] Cut036009013017007008008021005005044017001003
  Base = -> Chamfer008016008004001
  Tool = -> Box059
FEATURE [Part::Cut] Cut036009013017007008008021005005044017001004
  Base = -> Chamfer008016008005001
  Tool = -> Box060
FEATURE [Part::MultiFuse] Fusion036012039029022025
  Shapes = -> [Cut036009013017007008008021005005044017001003,Cut011069020007]
FEATURE [Part::MultiFuse] Fusion036012039029022026
  Shapes = -> [Cut011063,Cut036009013017007008008021005005044017001004]
FEATURE [Part::Cut] Cut036009013017007008008021005005044017001005
  Base = -> Fusion036012039029022025
  Tool = -> Cut036009013017007008008021005005044017001001
FEATURE [Part::MultiFuse] Fusion036012039029022027
  Shapes = -> [Cylinder067,Cylinder064]
FEATURE [Part::Cut] Cut036009013017007008008021005005044017001006
  Base = -> Cut036009013017007008008021005005044017001005
  Tool = -> Fusion036012039029022027
FEATURE [Part::MultiFuse] Fusion036012039029022028
  Shapes = -> [Cylinder065,Cylinder071,Cylinder066]
FEATURE [Part::Cut] Cut036009013017007008008021005005044017001007
  Base = -> Fusion036012039029022026
  Tool = -> Fusion036012039029022028
FEATURE [Part::MultiFuse] Fusion036012039029022029
  Shapes = -> [Cut036009013017007008008021005005044017001007,Chamfer008016008005002001]
FEATURE [Part::Cut] Cut036009013017007008008021005005044017001008
  Base = -> Cut036009013017007008008021005005044017001006
  Tool = -> Cylinder073001
FEATURE [Part::Box] Box064  label="Cube063"
  AttacherType = Attacher::AttachEngine3D
  Height = 1.5
  Length = 24
  Placement = pos=(-12,-11.15,10.56) rot=(0,0,1;0rad)
  Width = 5
FEATURE [Part::MultiFuse] Fusion036012039029022030
  Shapes = -> [Cut011069020011013,Box064]
FEATURE [Part::Box] Box065  label="Cube064"
  AttacherType = Attacher::AttachEngine3D
  Height = 3.5
  Length = 6
  Placement = pos=(-3,-11.15,9.56) rot=(0,0,1;0rad)
  Width = 6
FEATURE [Part::Fillet] Fillet001016004
  Base = -> Box065
  Edges = 2 edges r=1: [Edge3,Edge7]
FEATURE [Part::Cut] Cut036009013017007008008021005005044017001009  label="back-r2"
  Base = -> Fusion036012039029022030
  Tool = -> Fillet001016004
FEATURE [Part::Box] Box069  label="Cube068"
  AttacherType = Attacher::AttachEngine3D
  Height = 12
  Length = 2.6
  Placement = pos=(-24.8,-43.6,17) rot=(0,0,1;0rad)
  Width = 5
FEATURE [Part::Cut] Cut036009013017007008008021005005044017001010
  Base = -> Fillet001016001
  Tool = -> Box069
FEATURE [Part::Fillet] Fillet001016005
  Base = -> Cut036009013017007008008021005005044017001010
  Edges = 1 edges r=1: [Edge135]
FEATURE [Part::Fillet] Fillet001016006
  Base = -> Fillet001016005
  Edges = 1 edges r=0.4: [Edge82]
FEATURE [Part::Feature] Chamfer001001  label="orbitor-v2-mbdy"
  Placement = pos=(-0.1,-17.5,57.1) rot=(0,0,1;3.14159rad)
  shape: bbox 135.7 x 30.34 x 139 mm, 715 faces (baked)
